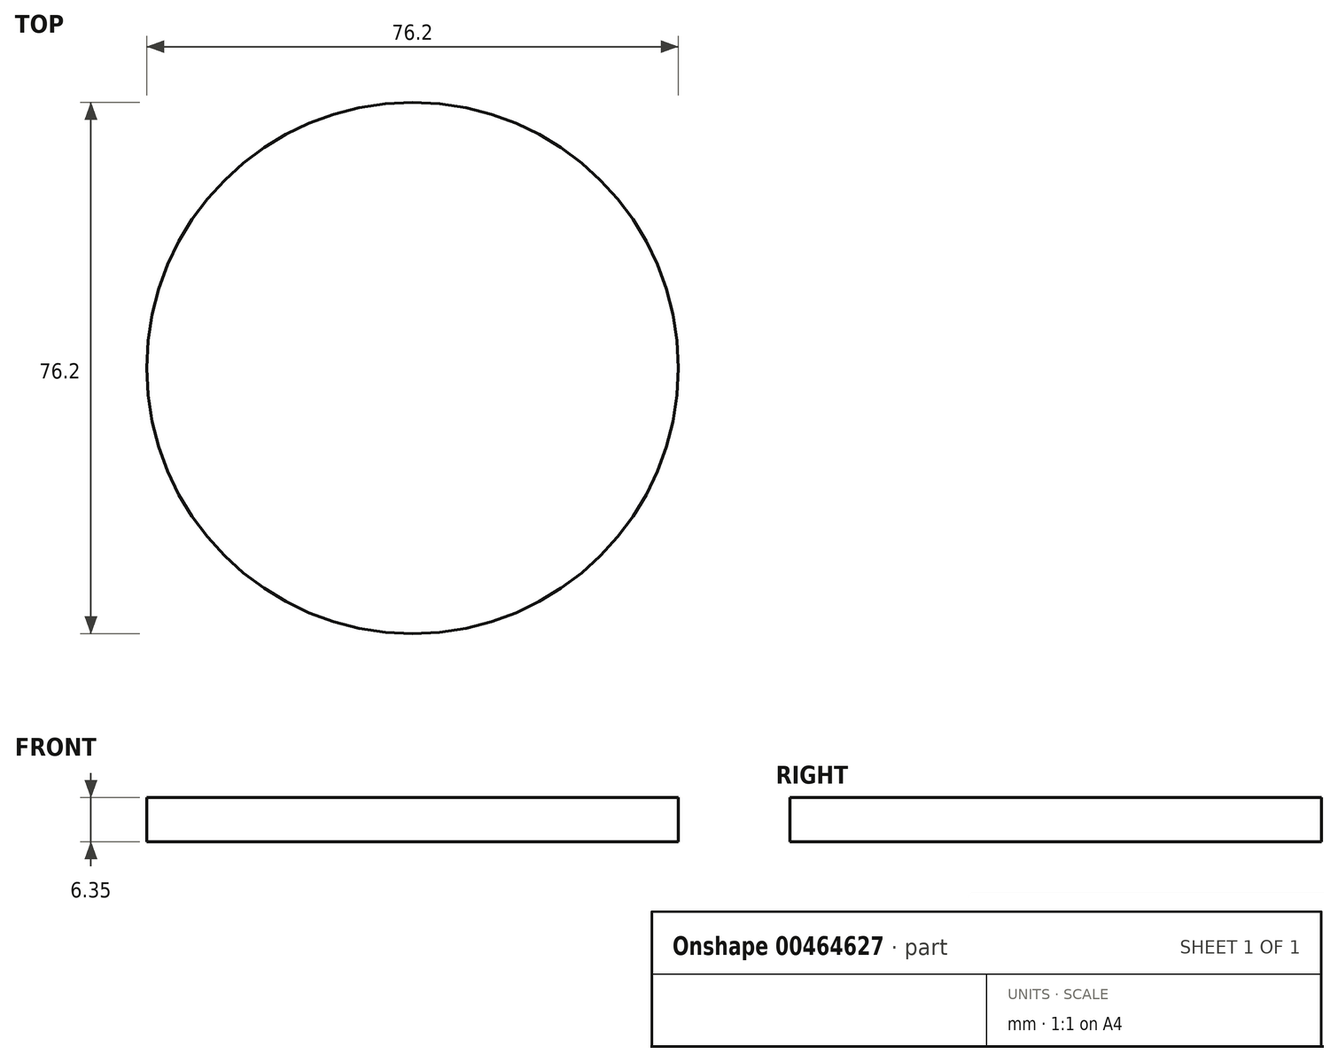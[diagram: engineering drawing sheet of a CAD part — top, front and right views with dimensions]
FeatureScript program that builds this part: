
annotation { "Feature Type Name" : "Feature", "Feature Type Description" : "" }
export const myFeature = defineFeature(function(context is Context, id is Id, definition is map)
    precondition{}
    {
        {
            var Q0;
            Q0=qCreatedBy(makeId("Top.planeOp"),FACE);
            var sketch = newSketch(context, id + "F0", { "sketchPlane" : qUnion([Q0])});
            skCircle(sketch, "E0", {"center": v(0, 0) * mm, "radius": 38.1 * mm});
            skSolve(sketch);
        }
        {
            var Q0;
            Q0 = qSketchRegion(id + "F0", true);
            extrude(context, id + "F1", {"entities" : qUnion([Q0]), "depth" : 6.35 * mm});
        }
    });
